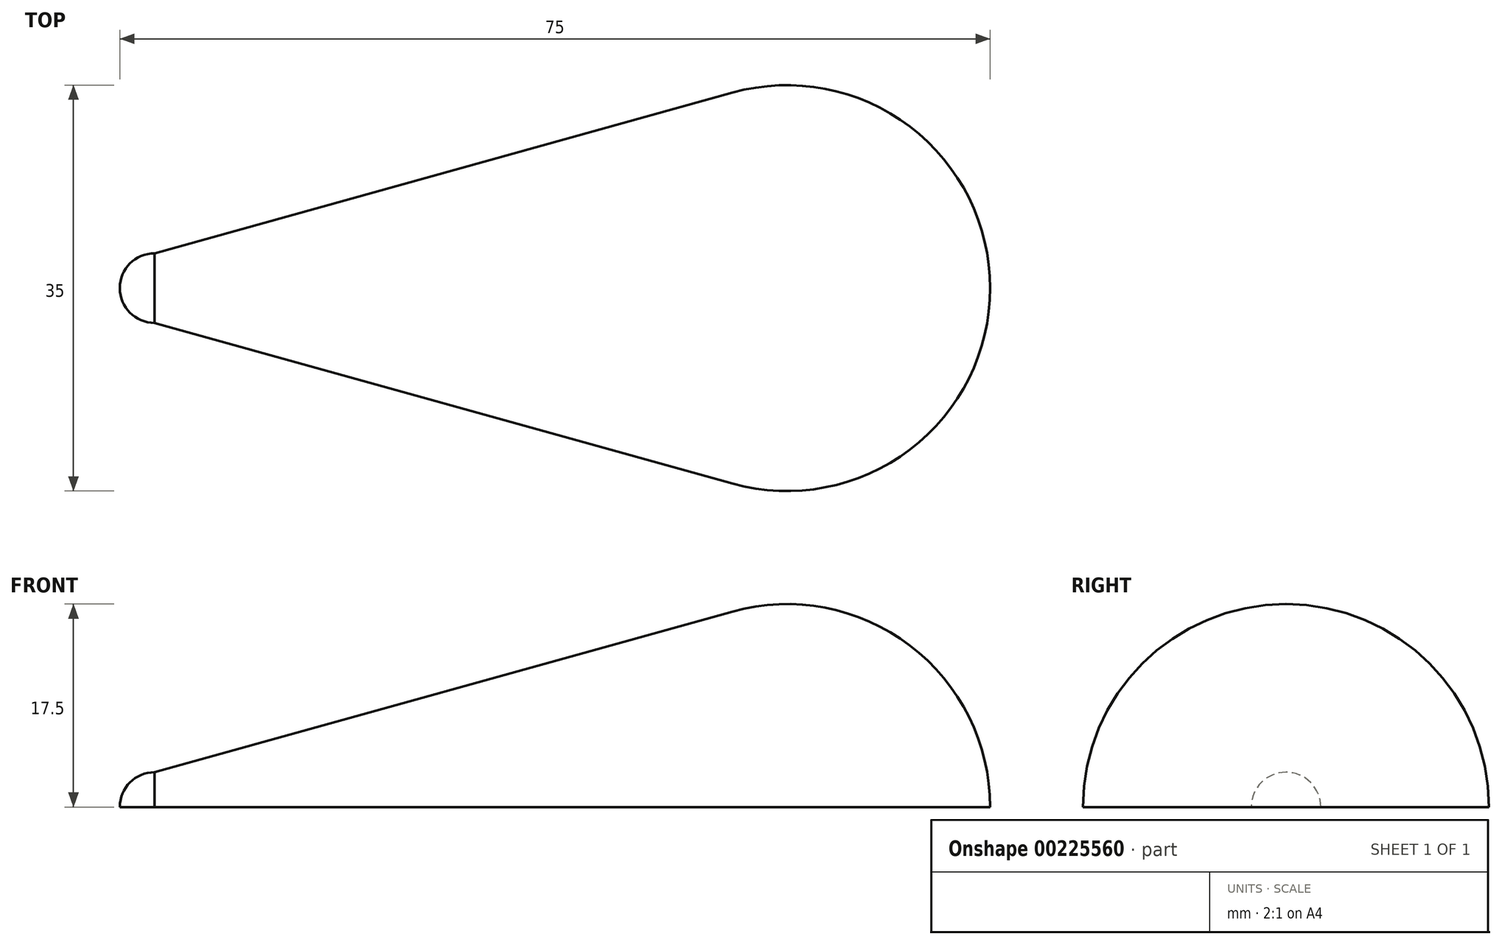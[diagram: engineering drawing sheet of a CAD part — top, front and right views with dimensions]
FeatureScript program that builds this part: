
annotation { "Feature Type Name" : "Feature", "Feature Type Description" : "" }
export const myFeature = defineFeature(function(context is Context, id is Id, definition is map)
    precondition{}
    {
        {
            var Q0;
            Q0=qCreatedBy(makeId("Front.planeOp"),FACE);
            var sketch = newSketch(context, id + "F0", { "sketchPlane" : qUnion([Q0])});
            skArc(sketch, "E0", {"start": v(72, 0) * mm, "mid": v(65.09, 13.93) * mm, "end": v(49.8, 16.86) * mm});
            skArc(sketch, "E1", {"start": v(0, 3) * mm, "mid": v(-2.12, 2.12) * mm, "end": v(-3, 0) * mm});
            skLineSegment(sketch, "E2", {"start": v(0, 3) * mm, "end": v(49.8, 16.86) * mm});
            skLineSegment(sketch, "E3", {"start": v(-3, 0) * mm, "end": v(72, 0) * mm});
            skLineSegment(sketch, "E4", {"start": v(9, 5.5) * mm, "end": v(9, 0) * mm, "construction": true});
            skLineSegment(sketch, "E5", {"start": v(13, 6.62) * mm, "end": v(13, 0) * mm, "construction": true});
            skSolve(sketch);
        }
        {
            var Q0;
            Q0=makeQuery(id+"F0.imprint","IMPRINT",FACE,{"disambiguationData":[TD([[makeQuery(id+"F0.imprint","IMPRINT",EDGE,{"derivedFrom":sQuery(id+"F0.wireOp",EDGE,"E0")}),1.0]])]});
            var Q1;
            Q1=sQuery(id+"F0.wireOp",EDGE,"E3");
            revolve(context, id + "F1", {"entities" : qUnion([Q0]), "axis" : qUnion([Q1]), "revolveType" : RevolveType.SYMMETRIC, "angle" : 180 * degree});
        }
    });
